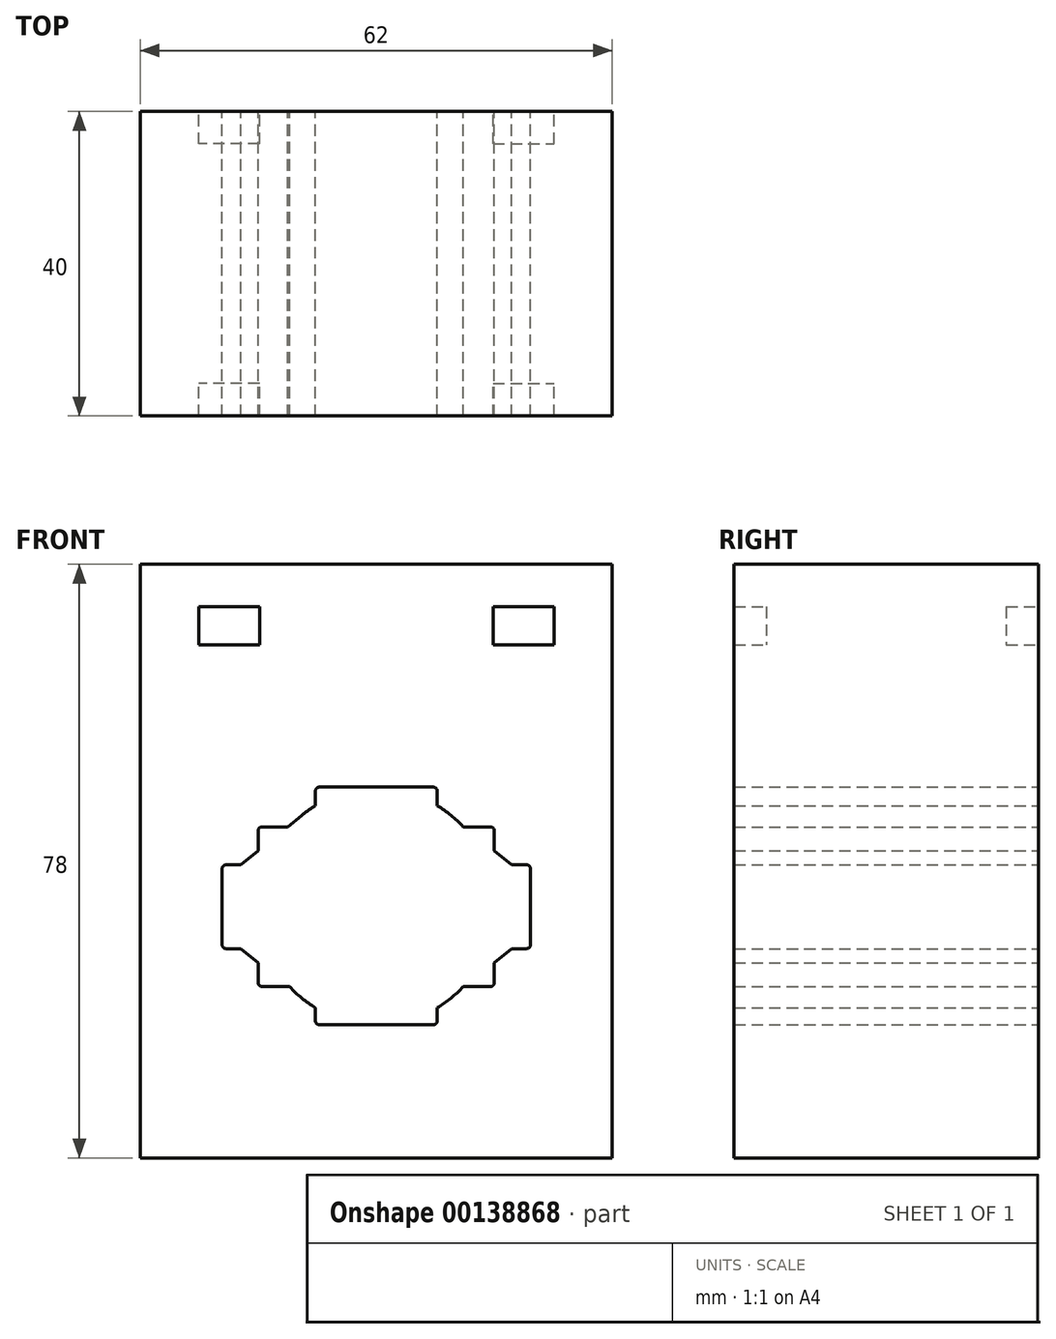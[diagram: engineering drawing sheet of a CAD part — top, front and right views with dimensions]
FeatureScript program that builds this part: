
annotation { "Feature Type Name" : "Feature", "Feature Type Description" : "" }
export const myFeature = defineFeature(function(context is Context, id is Id, definition is map)
    precondition{}
    {
        {
            var Q0;
            Q0=qCreatedBy(makeId("Front.planeOp"),FACE);
            var sketch = newSketch(context, id + "F0", { "sketchPlane" : qUnion([Q0])});
            skLineSegment(sketch, "E0.bottom", {"start": v(31, -39) * mm, "end": v(-31, -39) * mm});
            skLineSegment(sketch, "E0.top", {"start": v(31, 39) * mm, "end": v(-31, 39) * mm});
            skLineSegment(sketch, "E0.left", {"start": v(31, -39) * mm, "end": v(31, 39) * mm});
            skLineSegment(sketch, "E0.right", {"start": v(-31, -39) * mm, "end": v(-31, 39) * mm});
            skPoint(sketch, "E0.middle", {"position": v(0, 0) * mm});
            skLineSegment(sketch, "E1.bottom", {"start": v(15, -16.5) * mm, "end": v(11.4, -16.5) * mm});
            skLineSegment(sketch, "E1.top", {"start": v(15, 4.5) * mm, "end": v(11.4, 4.5) * mm});
            skLineSegment(sketch, "E1.left", {"start": v(15.5, -16) * mm, "end": v(15.5, -13.36) * mm});
            skLineSegment(sketch, "E1.right", {"start": v(-15.5, -16) * mm, "end": v(-15.5, -13.36) * mm});
            skLineSegment(sketch, "E2.bottom", {"start": v(19.75, -11.5) * mm, "end": v(17.78, -11.5) * mm});
            skLineSegment(sketch, "E2.top", {"start": v(19.75, -0.5) * mm, "end": v(17.78, -0.5) * mm});
            skLineSegment(sketch, "E2.left", {"start": v(20.25, -11) * mm, "end": v(20.25, -1) * mm});
            skLineSegment(sketch, "E2.right", {"start": v(-20.25, -11) * mm, "end": v(-20.25, -1) * mm});
            skLineSegment(sketch, "E3.bottom", {"start": v(7.5, -21.5) * mm, "end": v(-7.5, -21.5) * mm});
            skLineSegment(sketch, "E3.top", {"start": v(7.5, 9.72) * mm, "end": v(-7.5, 9.72) * mm});
            skLineSegment(sketch, "E3.right", {"start": v(-8, -21) * mm, "end": v(-8, -19.28) * mm});
            skLineSegment(sketch, "E4.trimOffspring", {"start": v(-11.4, 4.5) * mm, "end": v(-15, 4.5) * mm});
            skLineSegment(sketch, "E5.trimOffspring", {"start": v(-17.78, -0.5) * mm, "end": v(-19.75, -0.5) * mm});
            skLineSegment(sketch, "E6.trimOffspring", {"start": v(-17.78, -11.5) * mm, "end": v(-19.75, -11.5) * mm});
            skLineSegment(sketch, "E7.trimOffspring", {"start": v(-11.4, -16.5) * mm, "end": v(-15, -16.5) * mm});
            skLineSegment(sketch, "E8.trimOffspring", {"start": v(8, 7.28) * mm, "end": v(8, 9.22) * mm});
            skLineSegment(sketch, "E9.trimOffspring", {"start": v(15.5, 1.36) * mm, "end": v(15.5, 4) * mm});
            skLineSegment(sketch, "E10.trimOffspring", {"start": v(-8, 7.28) * mm, "end": v(-8, 9.22) * mm});
            skLineSegment(sketch, "E11.trimOffspring", {"start": v(-15.5, 1.36) * mm, "end": v(-15.5, 4) * mm});
            skLineSegment(sketch, "E12", {"start": v(8, -21) * mm, "end": v(8, -19.28) * mm});
            skArc(sketch, "E13", {"start": v(-8, 7.28) * mm, "mid": v(-9.8, 6) * mm, "end": v(-11.4, 4.5) * mm});
            skArc(sketch, "E14.trimOffspring", {"start": v(8, -19.28) * mm, "mid": v(9.8, -18) * mm, "end": v(11.4, -16.5) * mm});
            skArc(sketch, "E15.trimOffspring", {"start": v(-11.4, -16.5) * mm, "mid": v(-9.8, -18) * mm, "end": v(-8, -19.28) * mm});
            skArc(sketch, "E16.trimOffspring", {"start": v(11.4, 4.5) * mm, "mid": v(9.8, 6) * mm, "end": v(8, 7.28) * mm});
            skLineSegment(sketch, "E17", {"start": v(-9.8, 6) * mm, "end": v(-11.65, 4.5) * mm});
            skLineSegment(sketch, "E18.trimOffspring", {"start": v(-15.5, 1.36) * mm, "end": v(-17.78, -0.5) * mm});
            skLineSegment(sketch, "E19.MirrorCS", {"start": v(15.5, 1.36) * mm, "end": v(17.78, -0.5) * mm});
            skLineSegment(sketch, "E20.MirrorCS", {"start": v(15.5, -13.36) * mm, "end": v(17.78, -11.5) * mm});
            skLineSegment(sketch, "E21.MirrorCS", {"start": v(-15.5, -13.36) * mm, "end": v(-17.78, -11.5) * mm});
            skPoint(sketch, "E22.visualSharp", {"position": v(-8, 9.72) * mm});
            skArc(sketch, "E22.filletArc", {"start": v(-7.5, 9.72) * mm, "mid": v(-7.85, 9.57) * mm, "end": v(-8, 9.22) * mm});
            skPoint(sketch, "E23.visualSharp", {"position": v(8, 9.72) * mm});
            skArc(sketch, "E23.filletArc", {"start": v(8, 9.22) * mm, "mid": v(7.85, 9.57) * mm, "end": v(7.5, 9.72) * mm});
            skPoint(sketch, "E24.visualSharp", {"position": v(-15.5, 4.5) * mm});
            skArc(sketch, "E24.filletArc", {"start": v(-15, 4.5) * mm, "mid": v(-15.35, 4.35) * mm, "end": v(-15.5, 4) * mm});
            skPoint(sketch, "E25.visualSharp", {"position": v(-20.25, -0.5) * mm});
            skArc(sketch, "E25.filletArc", {"start": v(-19.75, -0.5) * mm, "mid": v(-20.1, -0.65) * mm, "end": v(-20.25, -1) * mm});
            skPoint(sketch, "E26.visualSharp", {"position": v(-20.25, -11.5) * mm});
            skArc(sketch, "E26.filletArc", {"start": v(-20.25, -11) * mm, "mid": v(-20.1, -11.35) * mm, "end": v(-19.75, -11.5) * mm});
            skPoint(sketch, "E27.visualSharp", {"position": v(-8, -21.5) * mm});
            skArc(sketch, "E27.filletArc", {"start": v(-8, -21) * mm, "mid": v(-7.85, -21.35) * mm, "end": v(-7.5, -21.5) * mm});
            skPoint(sketch, "E28.visualSharp", {"position": v(8, -21.5) * mm});
            skArc(sketch, "E28.filletArc", {"start": v(7.5, -21.5) * mm, "mid": v(7.85, -21.35) * mm, "end": v(8, -21) * mm});
            skPoint(sketch, "E29.visualSharp", {"position": v(15.5, -16.5) * mm});
            skArc(sketch, "E29.filletArc", {"start": v(15, -16.5) * mm, "mid": v(15.35, -16.35) * mm, "end": v(15.5, -16) * mm});
            skPoint(sketch, "E30.visualSharp", {"position": v(20.25, -11.5) * mm});
            skArc(sketch, "E30.filletArc", {"start": v(19.75, -11.5) * mm, "mid": v(20.1, -11.35) * mm, "end": v(20.25, -11) * mm});
            skPoint(sketch, "E31.visualSharp", {"position": v(20.25, -0.5) * mm});
            skArc(sketch, "E31.filletArc", {"start": v(20.25, -1) * mm, "mid": v(20.1, -0.65) * mm, "end": v(19.75, -0.5) * mm});
            skPoint(sketch, "E32.visualSharp", {"position": v(15.5, 4.5) * mm});
            skArc(sketch, "E32.filletArc", {"start": v(15.5, 4) * mm, "mid": v(15.35, 4.35) * mm, "end": v(15, 4.5) * mm});
            skPoint(sketch, "E33.visualSharp", {"position": v(-15.5, -16.5) * mm});
            skArc(sketch, "E33.filletArc", {"start": v(-15.5, -16) * mm, "mid": v(-15.35, -16.35) * mm, "end": v(-15, -16.5) * mm});
            skLineSegment(sketch, "E34.bottom", {"start": v(23.34, 28.4) * mm, "end": v(15.34, 28.4) * mm});
            skLineSegment(sketch, "E34.top", {"start": v(23.34, 33.4) * mm, "end": v(15.34, 33.4) * mm});
            skLineSegment(sketch, "E34.left", {"start": v(23.34, 28.4) * mm, "end": v(23.34, 33.4) * mm});
            skLineSegment(sketch, "E34.right", {"start": v(15.34, 28.4) * mm, "end": v(15.34, 33.4) * mm});
            skLineSegment(sketch, "E35.MirrorCS", {"start": v(-23.34, 28.4) * mm, "end": v(-23.34, 33.4) * mm});
            skLineSegment(sketch, "E36.MirrorCS", {"start": v(-23.34, 33.4) * mm, "end": v(-15.34, 33.4) * mm});
            skLineSegment(sketch, "E37.MirrorCS", {"start": v(-15.34, 28.4) * mm, "end": v(-15.34, 33.4) * mm});
            skLineSegment(sketch, "E38.MirrorCS", {"start": v(-23.34, 28.4) * mm, "end": v(-15.34, 28.4) * mm});
            skSolve(sketch);
        }
        {
            var Q0;
            Q0=makeQuery(id+"F0.imprint","IMPRINT",FACE,{"disambiguationData":[TD([[makeQuery(id+"F0.imprint","IMPRINT",EDGE,{"derivedFrom":sQuery(id+"F0.wireOp",EDGE,"E0.bottom")}),-1.0]])]});
            extrude(context, id + "F1", {"entities" : qUnion([Q0]), "depth" : 40 * mm, "symmetric" : true});
        }
        {
            var Q0;
            Q0=makeQuery(id+"F1.opExtrude","SWEPT_FACE",FACE,{"disambiguationData":[OSD([sQuery(id+"F0.wireOp",EDGE,"E0.top")])]});
            var sketch = newSketch(context, id + "F2", { "sketchPlane" : qUnion([Q0])});
            skPoint(sketch, "E39", {"position": v(0, 20) * mm});
            skPoint(sketch, "E40", {"position": v(0, 0) * mm});
            skLineSegment(sketch, "E41.bottom", {"start": v(27.18, 15.75) * mm, "end": v(-27.18, 15.75) * mm});
            skLineSegment(sketch, "E41.top", {"start": v(27.18, -15.75) * mm, "end": v(-27.18, -15.75) * mm});
            skLineSegment(sketch, "E41.left", {"start": v(27.18, 15.75) * mm, "end": v(27.18, -15.75) * mm});
            skLineSegment(sketch, "E41.right", {"start": v(-27.18, 15.75) * mm, "end": v(-27.18, -15.75) * mm});
            skSolve(sketch);
        }
        {
            var Q0;
            Q0=makeQuery(id+"F2.imprint","IMPRINT",FACE,{"disambiguationData":[TD([[makeQuery(id+"F2.imprint","IMPRINT",EDGE,{"derivedFrom":sQuery(id+"F2.wireOp",EDGE,"E41.bottom")}),1.0]])]});
            extrude(context, id + "F3", {"entities" : qUnion([Q0]), "operationType" : NewBodyOperationType.ADD, "oppositeDirection" : true, "depth" : 15 * mm});
        }
    });
